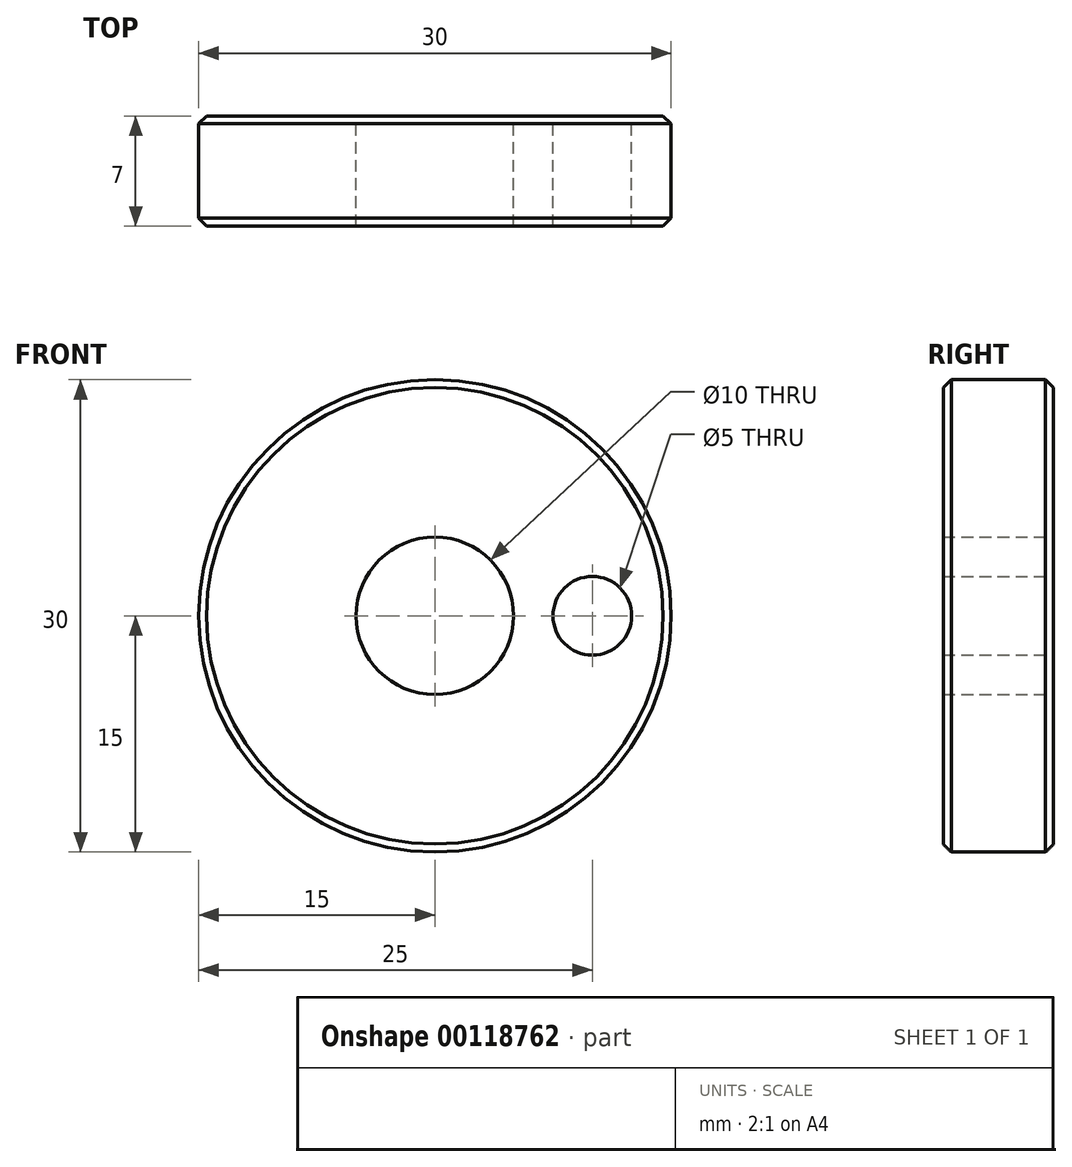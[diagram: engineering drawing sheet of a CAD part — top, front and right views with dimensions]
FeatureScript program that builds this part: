
annotation { "Feature Type Name" : "Feature", "Feature Type Description" : "" }
export const myFeature = defineFeature(function(context is Context, id is Id, definition is map)
    precondition{}
    {
        {
            var Q0;
            Q0=qCreatedBy(makeId("Front.planeOp"),FACE);
            var sketch = newSketch(context, id + "F0", { "sketchPlane" : qUnion([Q0])});
            skCircle(sketch, "E0", {"center": v(0, 0) * mm, "radius": 15 * mm});
            skCircle(sketch, "E1", {"center": v(0, 0) * mm, "radius": 5 * mm});
            skCircle(sketch, "E2", {"center": v(10, 0) * mm, "radius": 2.5 * mm});
            skSolve(sketch);
        }
        {
            var Q0;
            Q0 = qSketchRegion(id + "F0", true);
            extrude(context, id + "F1", {"entities" : qUnion([Q0]), "depth" : 7 * mm});
        }
        {
            var Q0;
            Q0=makeQuery(id+"F1.opExtrude","CAP_EDGE",EDGE,{"disambiguationData":[OSD([sQuery(id+"F0.wireOp",EDGE,"E0")])],"isStart":false});
            chamfer(context, id + "F2", {"entities" : qUnion([Q0]), "width" : 0.5 * mm, "tangentPropagation" : true});
        }
        {
            var Q0;
            Q0=makeQuery(id+"F1.opExtrude","CAP_EDGE",EDGE,{"disambiguationData":[OSD([sQuery(id+"F0.wireOp",EDGE,"E0")])],"isStart":true});
            chamfer(context, id + "F3", {"entities" : qUnion([Q0]), "width" : 0.5 * mm, "tangentPropagation" : true});
        }
    });
